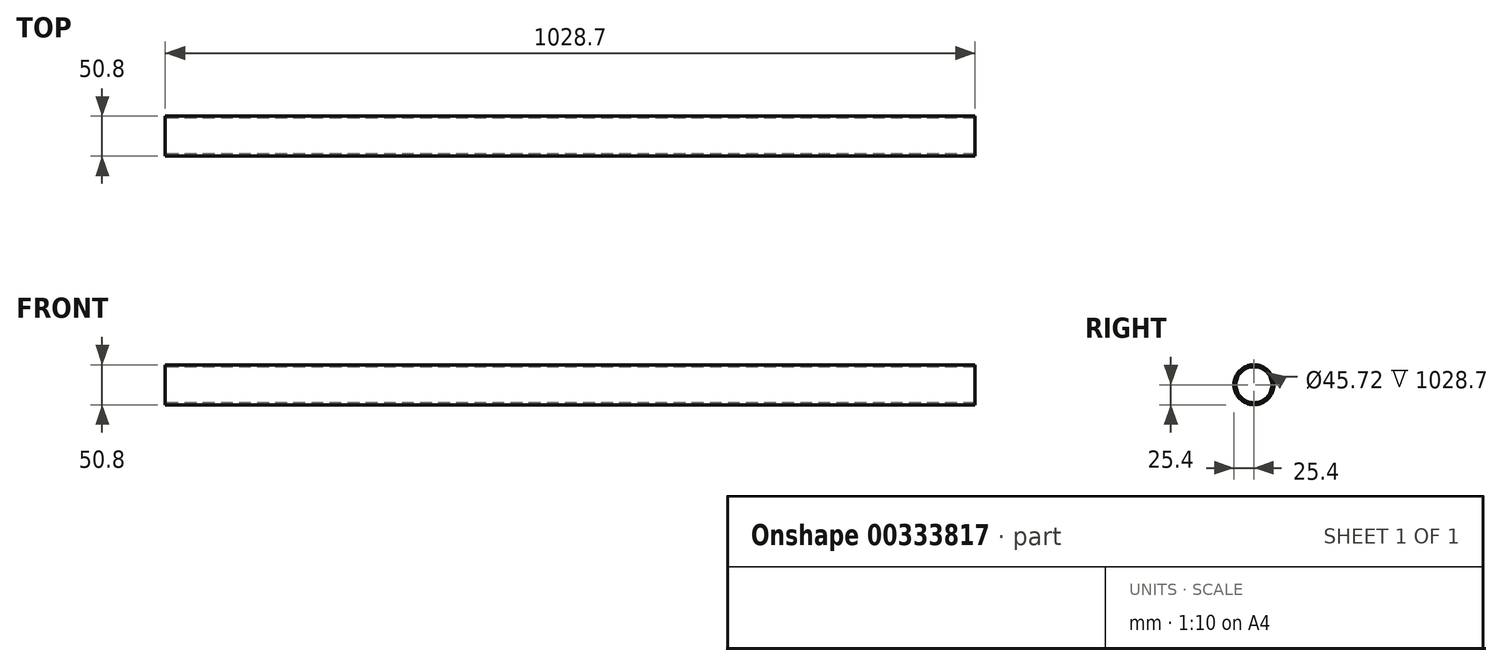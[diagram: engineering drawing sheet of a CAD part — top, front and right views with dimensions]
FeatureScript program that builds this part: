
annotation { "Feature Type Name" : "Feature", "Feature Type Description" : "" }
export const myFeature = defineFeature(function(context is Context, id is Id, definition is map)
    precondition{}
    {
        {
            var Q0;
            Q0=qCreatedBy(makeId("Right.planeOp"),FACE);
            var sketch = newSketch(context, id + "F0", { "sketchPlane" : qUnion([Q0])});
            skCircle(sketch, "E0", {"center": v(0, 0) * mm, "radius": 25.4 * mm});
            skCircle(sketch, "E1", {"center": v(0, 0) * mm, "radius": 22.86 * mm});
            skSolve(sketch);
        }
        {
            var Q0;
            Q0 = qSketchRegion(id + "F0", true);
            extrude(context, id + "F1", {"entities" : qUnion([Q0]), "depth" : 1028.7 * mm});
        }
    });
